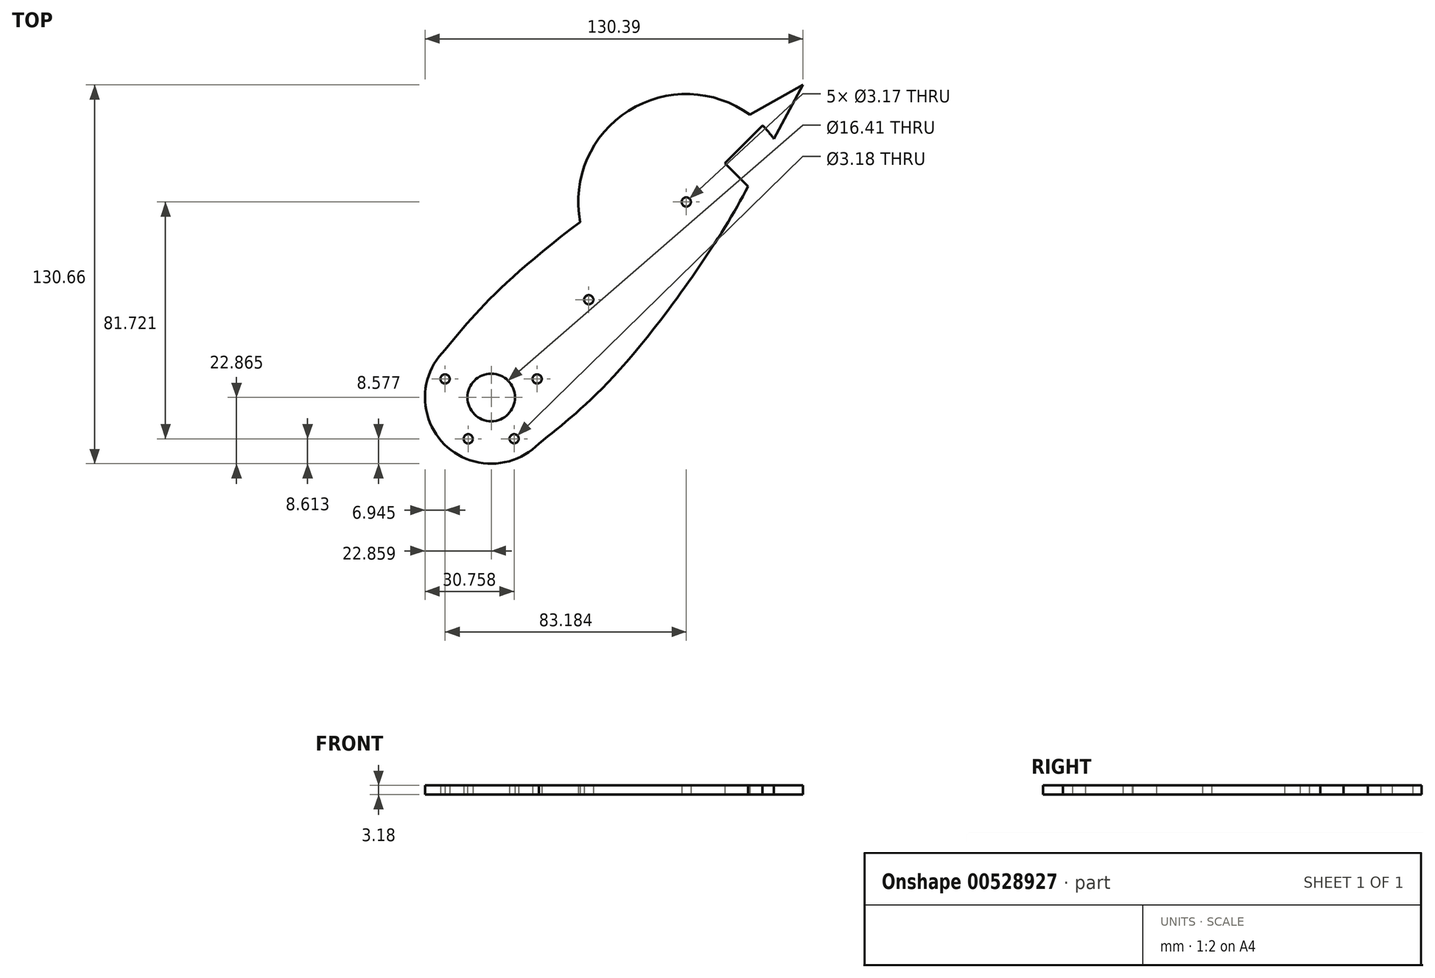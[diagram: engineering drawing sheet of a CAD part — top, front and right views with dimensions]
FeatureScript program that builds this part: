
annotation { "Feature Type Name" : "Feature", "Feature Type Description" : "" }
export const myFeature = defineFeature(function(context is Context, id is Id, definition is map)
    precondition{}
    {
        {
            var Q0;
            Q0=qCreatedBy(makeId("Top.planeOp"),FACE);
            var sketch = newSketch(context, id + "F0", { "sketchPlane" : qUnion([Q0])});
            skLineSegment(sketch, "E0.bottom", {"start": v(38.14, 38.06) * mm, "end": v(12.74, 38.06) * mm});
            skLineSegment(sketch, "E0.top", {"start": v(38.14, 12.66) * mm, "end": v(12.74, 12.66) * mm});
            skLineSegment(sketch, "E0.left", {"start": v(38.14, 38.06) * mm, "end": v(38.14, 12.66) * mm});
            skLineSegment(sketch, "E0.right", {"start": v(12.74, 38.06) * mm, "end": v(12.74, 12.66) * mm});
            skPoint(sketch, "E0.middle", {"position": v(25.44, 25.36) * mm});
            skCircle(sketch, "E1", {"center": v(9.52, 31.75) * mm, "radius": 1.59 * mm});
            skCircle(sketch, "E2", {"center": v(17.5, 11.08) * mm, "radius": 1.59 * mm});
            skCircle(sketch, "E3.MirrorC", {"center": v(33.34, 11.11) * mm, "radius": 1.59 * mm});
            skCircle(sketch, "E4.MirrorC", {"center": v(41.27, 31.75) * mm, "radius": 1.59 * mm});
            skLineSegment(sketch, "E5", {"start": v(25.44, 25.36) * mm, "end": v(92.7, 92.8) * mm});
            skCircle(sketch, "E6", {"center": v(92.7, 92.8) * mm, "radius": 1.59 * mm});
            skCircle(sketch, "E7", {"center": v(59.07, 59.08) * mm, "radius": 1.59 * mm});
            skCircle(sketch, "E8", {"center": v(25.44, 25.36) * mm, "radius": 22.86 * mm});
            skCircle(sketch, "E9", {"center": v(92.7, 92.8) * mm, "radius": 37.25 * mm});
            skCircle(sketch, "E10", {"center": v(25.44, 25.36) * mm, "radius": 8.2 * mm});
            skCircle(sketch, "E11", {"center": v(92.7, 92.8) * mm, "radius": 5 * mm});
            skLineSegment(sketch, "E12", {"start": v(92.7, 92.8) * mm, "end": v(119.02, 119.17) * mm});
            skFitSpline(sketch, "E13", {"points": [v(9.48, 41.73) * mm, v(42.84, 75.44) * mm, v(119.02, 119.17) * mm, v(76.42, 42.7) * mm, v(41.84, 9.44) * mm], "startDerivative": vector(107.94, 133.67) * mm, "endDerivative": vector(-133.4, -108.09) * mm});
            skLineSegment(sketch, "E14", {"start": v(98.26, 113.84) * mm, "end": v(132.97, 133.16) * mm});
            skLineSegment(sketch, "E15", {"start": v(119.02, 119.17) * mm, "end": v(132.97, 133.16) * mm});
            skLineSegment(sketch, "E16", {"start": v(132.97, 133.16) * mm, "end": v(114, 98.14) * mm});
            skLineSegment(sketch, "E17", {"start": v(114, 98.14) * mm, "end": v(98.26, 113.84) * mm});
            skSolve(sketch);
        }
        {
            var Q0;
            {var subQ4=sQuery(id+"F0.wireOp",EDGE,"E0.left");Q0=makeQuery(id+"F0.imprint","IMPRINT",FACE,{"disambiguationData":[TD([[makeQuery(id+"F0.imprint","IMPRINT",EDGE,{"derivedFrom":subQ4}),-1.0]])]});}
            var Q1;
            {var subQ2=sQuery(id+"F0.wireOp",EDGE,"E0.left");Q1=makeQuery(id+"F0.imprint","IMPRINT",FACE,{"disambiguationData":[TD([[makeQuery(id+"F0.imprint","IMPRINT",EDGE,{"derivedFrom":subQ2}),1.0]])]});}
            var Q2;
            {var subQ1=sQuery(id+"F0.wireOp",EDGE,"E5");var subQ5=sQuery(id+"F0.wireOp",EDGE,"E8");var subQ7=makeQuery(id+"F0.imprint","INTERSECT",VERTEX,{"derivedFrom":[subQ1,subQ5]});Q2=makeQuery(id+"F0.imprint","IMPRINT",FACE,{"disambiguationData":[TD([[makeQuery(id+"F0.imprint","IMPRINT",EDGE,{"disambiguationData":[TD([[subQ7,-1.0]])],"derivedFrom":subQ1}),-1.0]])]});}
            var Q3;
            {var subQ1=sQuery(id+"F0.wireOp",EDGE,"E5");var subQ7=sQuery(id+"F0.wireOp",EDGE,"E8");var subQ10=makeQuery(id+"F0.imprint","INTERSECT",VERTEX,{"derivedFrom":[subQ1,subQ7]});Q3=makeQuery(id+"F0.imprint","IMPRINT",FACE,{"disambiguationData":[TD([[makeQuery(id+"F0.imprint","IMPRINT",EDGE,{"disambiguationData":[TD([[subQ10,-1.0]])],"derivedFrom":subQ1}),1.0]])]});}
            var Q4;
            {var subQ1=sQuery(id+"F0.wireOp",EDGE,"E5");var subQ6=sQuery(id+"F0.wireOp",EDGE,"E9");var subQ8=makeQuery(id+"F0.imprint","INTERSECT",VERTEX,{"derivedFrom":[subQ1,subQ6]});Q4=makeQuery(id+"F0.imprint","IMPRINT",FACE,{"disambiguationData":[TD([[makeQuery(id+"F0.imprint","IMPRINT",EDGE,{"disambiguationData":[TD([[subQ8,-1.0]])],"derivedFrom":subQ1}),-1.0]])]});}
            var Q5;
            {var subQ0=sQuery(id+"F0.wireOp",EDGE,"E11");var subQ1=sQuery(id+"F0.wireOp",EDGE,"E5");var subQ2=makeQuery(id+"F0.imprint","INTERSECT",VERTEX,{"derivedFrom":[subQ1,subQ0]});Q5=makeQuery(id+"F0.imprint","IMPRINT",FACE,{"disambiguationData":[TD([[makeQuery(id+"F0.imprint","IMPRINT",EDGE,{"disambiguationData":[TD([[subQ2,-1.0]])],"derivedFrom":subQ1}),-1.0]])]});}
            var Q6;
            {var subQ0=sQuery(id+"F0.wireOp",EDGE,"E11");var subQ1=sQuery(id+"F0.wireOp",EDGE,"E5");var subQ2=makeQuery(id+"F0.imprint","INTERSECT",VERTEX,{"derivedFrom":[subQ1,subQ0]});Q6=makeQuery(id+"F0.imprint","IMPRINT",FACE,{"disambiguationData":[TD([[makeQuery(id+"F0.imprint","IMPRINT",EDGE,{"disambiguationData":[TD([[subQ2,-1.0]])],"derivedFrom":subQ1}),1.0]])]});}
            var Q7;
            {var subQ1=sQuery(id+"F0.wireOp",EDGE,"E5");var subQ6=sQuery(id+"F0.wireOp",EDGE,"E9");var subQ8=makeQuery(id+"F0.imprint","INTERSECT",VERTEX,{"derivedFrom":[subQ1,subQ6]});Q7=makeQuery(id+"F0.imprint","IMPRINT",FACE,{"disambiguationData":[TD([[makeQuery(id+"F0.imprint","IMPRINT",EDGE,{"disambiguationData":[TD([[subQ8,-1.0]])],"derivedFrom":subQ1}),1.0]])]});}
            var Q8;
            {var subQ0=sQuery(id+"F0.wireOp",EDGE,"E13");var subQ2=sQuery(id+"F0.wireOp",EDGE,"E9");var subQ4=makeQuery(id+"F0.imprint","INTERSECT",VERTEX,{"disambiguationData":[OD(0.0)],"derivedFrom":[subQ2,subQ0]});Q8=makeQuery(id+"F0.imprint","IMPRINT",FACE,{"disambiguationData":[TD([[makeQuery(id+"F0.imprint","IMPRINT",EDGE,{"disambiguationData":[TD([[subQ4,-1.0]])],"derivedFrom":subQ0}),-1.0]])]});}
            var Q9;
            {var subQ1=sQuery(id+"F0.wireOp",EDGE,"E12");var subQ3=sQuery(id+"F0.wireOp",EDGE,"E17");var subQ4=makeQuery(id+"F0.imprint","INTERSECT",VERTEX,{"derivedFrom":[subQ1,subQ3]});Q9=makeQuery(id+"F0.imprint","IMPRINT",FACE,{"disambiguationData":[TD([[makeQuery(id+"F0.imprint","IMPRINT",EDGE,{"disambiguationData":[TD([[subQ4,-1.0]])],"derivedFrom":subQ3}),-1.0]])]});}
            var Q10;
            {var subQ0=sQuery(id+"F0.wireOp",EDGE,"E15");Q10=makeQuery(id+"F0.imprint","IMPRINT",FACE,{"disambiguationData":[TD([[makeQuery(id+"F0.imprint","IMPRINT",EDGE,{"derivedFrom":subQ0}),1.0]])]});}
            var Q11;
            {var subQ5=sQuery(id+"F0.wireOp",EDGE,"E15");Q11=makeQuery(id+"F0.imprint","IMPRINT",FACE,{"disambiguationData":[TD([[makeQuery(id+"F0.imprint","IMPRINT",EDGE,{"derivedFrom":subQ5}),-1.0]])]});}
            var Q12;
            {var subQ0=sQuery(id+"F0.wireOp",EDGE,"E13");var subQ1=sQuery(id+"F0.wireOp",EDGE,"E9");var subQ2=makeQuery(id+"F0.imprint","INTERSECT",VERTEX,{"disambiguationData":[OD(0.0)],"derivedFrom":[subQ1,subQ0]});Q12=makeQuery(id+"F0.imprint","IMPRINT",FACE,{"disambiguationData":[TD([[makeQuery(id+"F0.imprint","IMPRINT",EDGE,{"disambiguationData":[TD([[subQ2,1.0]])],"derivedFrom":subQ1}),1.0]])]});}
            var Q13;
            {var subQ1=sQuery(id+"F0.wireOp",EDGE,"E9");var subQ3=sQuery(id+"F0.wireOp",EDGE,"E14");var subQ4=makeQuery(id+"F0.imprint","INTERSECT",VERTEX,{"derivedFrom":[subQ1,subQ3]});Q13=makeQuery(id+"F0.imprint","IMPRINT",FACE,{"disambiguationData":[TD([[makeQuery(id+"F0.imprint","IMPRINT",EDGE,{"disambiguationData":[TD([[subQ4,1.0]])],"derivedFrom":subQ3}),-1.0]])]});}
            extrude(context, id + "F1", {"entities" : qUnion([Q0, Q1, Q2, Q3, Q4, Q5, Q6, Q7, Q8, Q9, Q10, Q11, Q12, Q13]), "depth" : 3.17 * mm, "offsetDistance" : 25.4 * mm});
        }
    });
